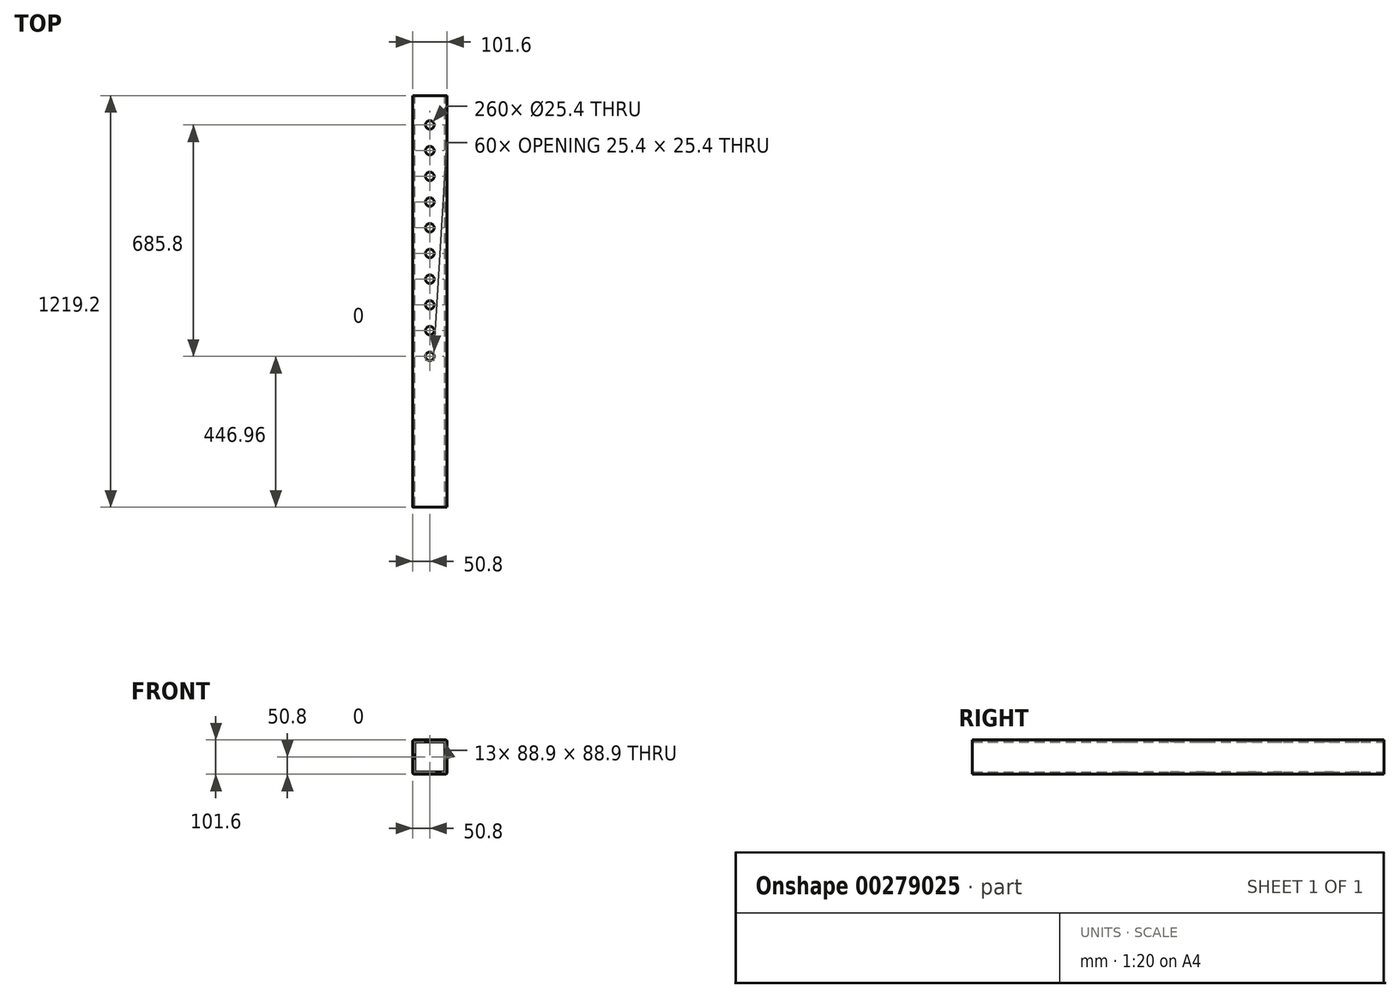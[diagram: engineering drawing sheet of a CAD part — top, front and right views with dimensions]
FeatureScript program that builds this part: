
annotation { "Feature Type Name" : "Feature", "Feature Type Description" : "" }
export const myFeature = defineFeature(function(context is Context, id is Id, definition is map)
    precondition{}
    {
        {
            var Q0;
            Q0=qCreatedBy(makeId("Front.planeOp"),FACE);
            var sketch = newSketch(context, id + "F0", { "sketchPlane" : qUnion([Q0])});
            skLineSegment(sketch, "E0.bottom", {"start": v(50.8, 50.8) * mm, "end": v(-50.8, 50.8) * mm});
            skLineSegment(sketch, "E0.top", {"start": v(50.8, -50.8) * mm, "end": v(-50.8, -50.8) * mm});
            skLineSegment(sketch, "E0.left", {"start": v(50.8, 50.8) * mm, "end": v(50.8, -50.8) * mm});
            skLineSegment(sketch, "E0.right", {"start": v(-50.8, 50.8) * mm, "end": v(-50.8, -50.8) * mm});
            skPoint(sketch, "E0.middle", {"position": v(0, 0) * mm});
            skLineSegment(sketch, "E1.0", {"start": v(44.45, 44.45) * mm, "end": v(-44.45, 44.45) * mm});
            skLineSegment(sketch, "E1.1", {"start": v(44.45, 44.45) * mm, "end": v(44.45, -44.45) * mm});
            skLineSegment(sketch, "E1.2", {"start": v(44.45, -44.45) * mm, "end": v(-44.45, -44.45) * mm});
            skLineSegment(sketch, "E1.3", {"start": v(-44.45, 44.45) * mm, "end": v(-44.45, -44.45) * mm});
            skSolve(sketch);
        }
        {
            var Q0;
            Q0=makeQuery(id+"F0.imprint","IMPRINT",FACE,{"disambiguationData":[TD([[makeQuery(id+"F0.imprint","IMPRINT",EDGE,{"derivedFrom":sQuery(id+"F0.wireOp",EDGE,"E0.bottom")}),1.0]])]});
            extrude(context, id + "F1", {"entities" : qUnion([Q0]), "endBound" : BoundingType.SYMMETRIC, "depth" : 1219.2 * mm});
        }
        {
            var Q0;
            Q0=makeQuery(id+"F1.opExtrude","SWEPT_EDGE",EDGE,{"disambiguationData":[OSD([sQuery(id+"F0.wireOp",EDGE,"E0.bottom"),sQuery(id+"F0.wireOp",EDGE,"E0.right")])]});
            var Q1;
            Q1=makeQuery(id+"F1.opExtrude","SWEPT_EDGE",EDGE,{"disambiguationData":[OSD([sQuery(id+"F0.wireOp",EDGE,"E0.bottom"),sQuery(id+"F0.wireOp",EDGE,"E0.left")])]});
            var Q2;
            Q2=makeQuery(id+"F1.opExtrude","SWEPT_EDGE",EDGE,{"disambiguationData":[OSD([sQuery(id+"F0.wireOp",EDGE,"E0.top"),sQuery(id+"F0.wireOp",EDGE,"E0.left")])]});
            var Q3;
            Q3=makeQuery(id+"F1.opExtrude","SWEPT_EDGE",EDGE,{"disambiguationData":[OSD([sQuery(id+"F0.wireOp",EDGE,"E0.top"),sQuery(id+"F0.wireOp",EDGE,"E0.right")])]});
            fillet(context, id + "F2", {"entities" : qUnion([Q0, Q1, Q2, Q3]), "radius" : 5.08 * mm, "tangentPropagation" : true, "allowEdgeOverflow" : false});
        }
        {
            var Q0;
            Q0=makeQuery(id+"F1.opExtrude","SWEPT_FACE",FACE,{"disambiguationData":[OSD([sQuery(id+"F0.wireOp",EDGE,"E0.bottom")])]});
            var sketch = newSketch(context, id + "F3", { "sketchPlane" : qUnion([Q0])});
            skLineSegment(sketch, "E2", {"start": v(0, 609.6) * mm, "end": v(0, 444.42) * mm, "construction": true});
            skCircle(sketch, "E3", {"center": v(0, 523.16) * mm, "radius": 12.7 * mm});
            skCircle(sketch, "E4.0.1.0", {"center": v(0, 446.96) * mm, "radius": 12.7 * mm});
            skCircle(sketch, "E4.0.2.0", {"center": v(0, 370.76) * mm, "radius": 12.7 * mm});
            skCircle(sketch, "E4.0.3.0", {"center": v(0, 294.56) * mm, "radius": 12.7 * mm});
            skCircle(sketch, "E4.0.4.0", {"center": v(0, 218.36) * mm, "radius": 12.7 * mm});
            skCircle(sketch, "E4.0.5.0", {"center": v(0, 142.16) * mm, "radius": 12.7 * mm});
            skCircle(sketch, "E4.0.6.0", {"center": v(0, 65.96) * mm, "radius": 12.7 * mm});
            skCircle(sketch, "E4.0.7.0", {"center": v(0, -10.24) * mm, "radius": 12.7 * mm});
            skCircle(sketch, "E4.0.8.0", {"center": v(0, -86.44) * mm, "radius": 12.7 * mm});
            skCircle(sketch, "E4.0.9.0", {"center": v(0, -162.64) * mm, "radius": 12.7 * mm});
            skLineSegment(sketch, "E4.direction1", {"start": v(0, 523.16) * mm, "end": v(25.4, 523.16) * mm, "construction": true});
            skLineSegment(sketch, "E4.direction2", {"start": v(0, 523.16) * mm, "end": v(0, 446.96) * mm, "construction": true});
            skSolve(sketch);
        }
        {
            var Q0;
            Q0 = qSketchRegion(id + "F3", true);
            extrude(context, id + "F4", {"entities" : qUnion([Q0]), "operationType" : NewBodyOperationType.REMOVE, "endBound" : BoundingType.THROUGH_ALL, "oppositeDirection" : true, "depth" : 25.4 * mm});
        }
    });
